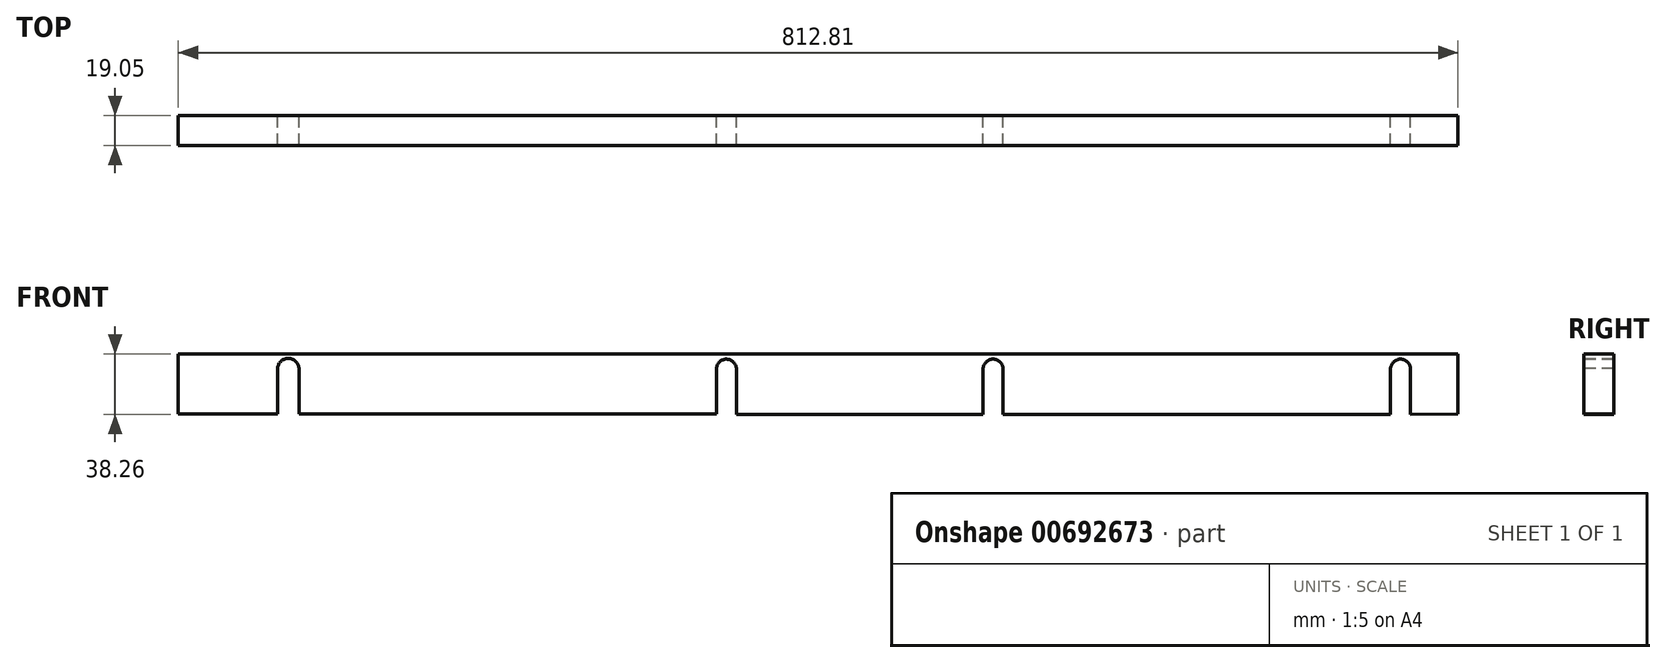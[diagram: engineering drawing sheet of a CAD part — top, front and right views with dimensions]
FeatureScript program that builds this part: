
annotation { "Feature Type Name" : "Feature", "Feature Type Description" : "" }
export const myFeature = defineFeature(function(context is Context, id is Id, definition is map)
    precondition{}
    {
        {
            var Q0;
            Q0=qCreatedBy(makeId("Front.planeOp"),FACE);
            var sketch = newSketch(context, id + "F0", { "sketchPlane" : qUnion([Q0])});
            skLineSegment(sketch, "E0", {"start": v(-400.82, 0) * mm, "end": v(411.98, 0) * mm});
            skLineSegment(sketch, "E1", {"start": v(-400.82, 0) * mm, "end": v(-400.82, -31.75) * mm});
            skLineSegment(sketch, "E2", {"start": v(412, -31.75) * mm, "end": v(411.98, 0) * mm});
            skPoint(sketch, "E3", {"position": v(-330.96, -9.52) * mm});
            skPoint(sketch, "E4", {"position": v(-53.14, -9.52) * mm});
            skPoint(sketch, "E5", {"position": v(116.72, -9.52) * mm});
            skPoint(sketch, "E6", {"position": v(375.48, -9.52) * mm});
            skLineSegment(sketch, "E7", {"start": v(-324.16, -31.74) * mm, "end": v(-59.04, -31.74) * mm});
            skLineSegment(sketch, "E8", {"start": v(-46.4, -8.74) * mm, "end": v(-46.4, -31.82) * mm});
            skLineSegment(sketch, "E9", {"start": v(-46.4, -31.82) * mm, "end": v(110.36, -31.82) * mm});
            skLineSegment(sketch, "E10", {"start": v(381.82, -31.91) * mm, "end": v(412, -31.75) * mm});
            skLineSegment(sketch, "E11", {"start": v(369.15, -31.83) * mm, "end": v(123.07, -31.83) * mm});
            skLineSegment(sketch, "E12", {"start": v(-59.04, -9.56) * mm, "end": v(-59.04, -31.74) * mm});
            skLineSegment(sketch, "E13", {"start": v(-400.82, -31.75) * mm, "end": v(-337.75, -31.75) * mm});
            skArc(sketch, "E14", {"start": v(-46.4, -8.74) * mm, "mid": v(-53.1, -3.22) * mm, "end": v(-59.04, -9.56) * mm});
            skArc(sketch, "E15", {"start": v(123.07, -9.52) * mm, "mid": v(116.72, -3.17) * mm, "end": v(110.37, -9.52) * mm});
            skLineSegment(sketch, "E16", {"start": v(123.07, -9.52) * mm, "end": v(123.07, -31.83) * mm});
            skLineSegment(sketch, "E17", {"start": v(110.37, -9.52) * mm, "end": v(110.36, -31.82) * mm});
            skArc(sketch, "E18", {"start": v(381.81, -9.52) * mm, "mid": v(375.48, -3.2) * mm, "end": v(369.15, -9.52) * mm});
            skLineSegment(sketch, "E19", {"start": v(381.81, -9.52) * mm, "end": v(381.82, -31.91) * mm});
            skLineSegment(sketch, "E20", {"start": v(369.15, -9.52) * mm, "end": v(369.15, -31.83) * mm});
            skArc(sketch, "E21", {"start": v(-324.15, -9.52) * mm, "mid": v(-330.96, -2.72) * mm, "end": v(-337.76, -9.52) * mm});
            skLineSegment(sketch, "E22", {"start": v(-324.15, -9.52) * mm, "end": v(-324.16, -31.74) * mm});
            skLineSegment(sketch, "E23", {"start": v(-337.76, -9.53) * mm, "end": v(-337.75, -31.75) * mm});
            skSolve(sketch);
        }
        {
            var Q0;
            Q0=makeQuery(id+"F0.imprint","IMPRINT",FACE,{"disambiguationData":[TD([[makeQuery(id+"F0.imprint","IMPRINT",EDGE,{"derivedFrom":sQuery(id+"F0.wireOp",EDGE,"E0")}),-1.0]])]});
            extrude(context, id + "F1", {"entities" : qUnion([Q0]), "depth" : 19.05 * mm, "offsetDistance" : 25.4 * mm});
        }
        {
            var Q0;
            Q0=makeQuery(id+"F1.opExtrude","SWEPT_FACE",FACE,{"disambiguationData":[OSD([sQuery(id+"F0.wireOp",EDGE,"E13")])]});
            var Q1;
            Q1=makeQuery(id+"F1.opExtrude","SWEPT_FACE",FACE,{"disambiguationData":[OSD([sQuery(id+"F0.wireOp",EDGE,"E7")])]});
            var Q2;
            Q2=makeQuery(id+"F1.opExtrude","SWEPT_FACE",FACE,{"disambiguationData":[OSD([sQuery(id+"F0.wireOp",EDGE,"E9")])]});
            var Q3;
            Q3=makeQuery(id+"F1.opExtrude","SWEPT_FACE",FACE,{"disambiguationData":[OSD([sQuery(id+"F0.wireOp",EDGE,"E11")])]});
            var Q4;
            Q4=makeQuery(id+"F1.opExtrude","SWEPT_FACE",FACE,{"disambiguationData":[OSD([sQuery(id+"F0.wireOp",EDGE,"E10")])]});
            extrude(context, id + "F2", {"entities" : qUnion([Q0, Q1, Q2, Q3, Q4]), "operationType" : NewBodyOperationType.ADD, "depth" : 6.35 * mm, "offsetDistance" : 25.4 * mm});
        }
    });
